# Revit family: Faucet-Bidet-DXV-Ashbee-D3510133X_Series
name_source: partatom
category: Plumbing Fixtures
revit_build: Autodesk Revit 2014 (Build: 20130308_1515(x64)
units: mm (PartAtom-declared; Revit-internal decimal feet)

## types (6) — shared parameters
Assembly Code = D2020300
CW Connection = Yes
CWFU = 10
Cold Water Connection Diameter = 1/2"
Default Elevation = 0"
Description = Ashbee Three-Hole  Bidet Faucet
HW Connection = Yes
HWFU = 10
Height = 6 1/16"
Hot Water Connection Diameter = 1"
Installation Type = Deck Mounted
Length = 13"
Manufacturer = DXV
Price = Prices may vary. Please consult Manufacturer Representative for most up-to-date price list.
Product Documentation Link = https://dxv01.blob.core.windows.net
Product Page URL = https://www.dxv.com
Revised Date = 21/09/2017
URL = http://www.dxv.com
Vent Connection = No
WFU = 10
Warranty Documentation Link = https://www.dxv.com
Waste Connection = No
Width = 8"

## per-type parameters (varying)
| type | ADA Compliant | Cross Handle Option | Finish | Lever Handle Option | Material |
| D35101334.144 | No | Yes | Metal-DXV-144-Brushed Nickel | No | Metal-DXV-144-Brushed Nickel |
| D35101334.100 | No | Yes | Metal-DXV-100-Polished Chrome | No | Metal-DXV-100-Polished Chrome |
| D35101334.150 | No | Yes | Metal-DXV-150-Platinum Nickel | No | Metal-DXV-150-Platinum Nickel |
| D35101330.100 | Yes | No | Metal-DXV-100-Polished Chrome | Yes | Metal-DXV-100-Polished Chrome |
| D35101330.144 | Yes | No | Metal-DXV-144-Brushed Nickel | Yes | Metal-DXV-144-Brushed Nickel |
| D35101330.150 | Yes | No | Metal-DXV-150-Platinum Nickel | Yes | Metal-DXV-150-Platinum Nickel |

note: column(s) folded — value = type name in every type: Model

## geometry (parser evidence)
native form markers: Sweep x2
no freeform markers — native parametric forms only
